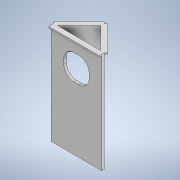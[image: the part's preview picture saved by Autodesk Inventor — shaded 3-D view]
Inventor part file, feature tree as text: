
AUTODESK INVENTOR PART (.ipt)
format: ipt  version: 2020 (Build 240168000, 168)  size: 167,936 bytes
history: native  units: mm
features: extrude x4, sketch x4
ambient origin geometry x8: Origin, YZ Plane, XZ Plane, XY Plane, X Axis, Y Axis, Z Axis, Center Point
bodies: Solid1 (feature_tree)
feature tree (8):
  extrude  "Extrusion1"  Depth=200.0mm
  extrude  "Extrusion2"  TaperAngle=45.0deg  [1 undecoded]
  extrude  "Extrusion6"  Depth=5.0mm
  extrude  "Extrusion9"  Depth=50.0mm
  sketch  "Sketch1"  dims[d0=100.0mm d1=200.0mm]
  sketch  "Sketch2"  dims[d2=5.0mm d3=0.0mm d4=45.0deg]
  sketch  "Sketch6"  dims[d5=5.0mm d6=5.0mm]
  sketch  "Sketch10"  dims[d7=45.0mm d8=0.0mm d21=50.0mm d22=50.0mm d23=20.0mm d24=5.0mm d25=0.0mm d33=5.0mm d34=5.0mm d35=5.0mm d36=3.0mm d37=0.0mm]
note: 1 required parameter value undecoded (feature->parameter linkage not recoverable at this tier; creation-order binding heuristic only, values carry confidence <= 0.55)
